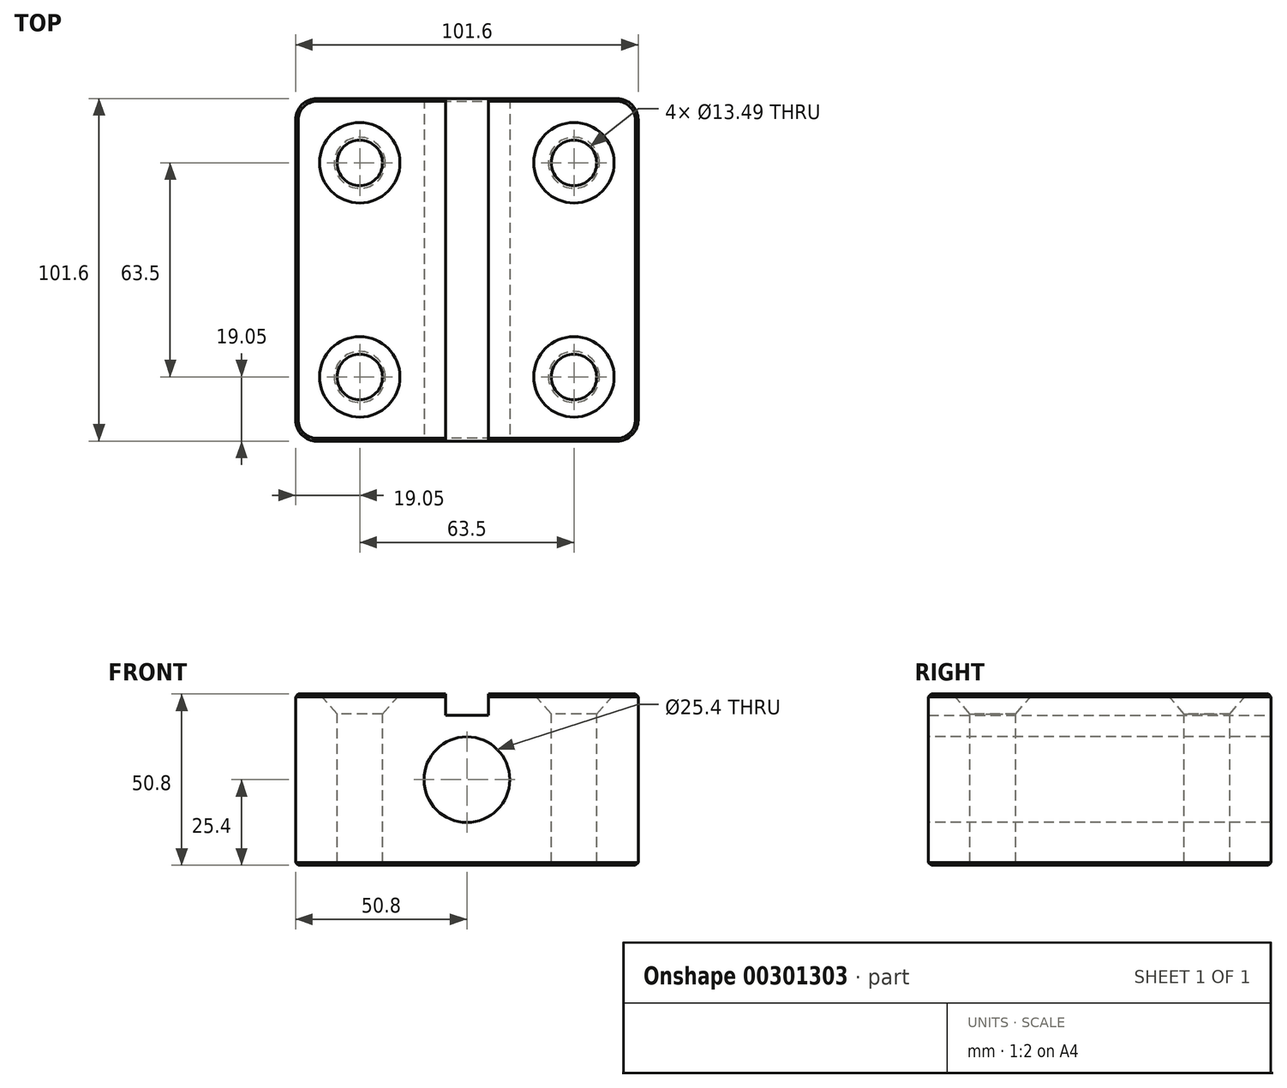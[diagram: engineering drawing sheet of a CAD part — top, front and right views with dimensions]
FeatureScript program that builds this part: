
annotation { "Feature Type Name" : "Feature", "Feature Type Description" : "" }
export const myFeature = defineFeature(function(context is Context, id is Id, definition is map)
    precondition{}
    {
        {
            var Q0;
            Q0=qCreatedBy(makeId("Front.planeOp"),FACE);
            var sketch = newSketch(context, id + "F0", { "sketchPlane" : qUnion([Q0])});
            skLineSegment(sketch, "E0.bottom", {"start": v(-50.8, 25.4) * mm, "end": v(50.8, 25.4) * mm});
            skLineSegment(sketch, "E0.top", {"start": v(-50.8, -25.4) * mm, "end": v(50.8, -25.4) * mm});
            skLineSegment(sketch, "E0.left", {"start": v(-50.8, 25.4) * mm, "end": v(-50.8, -25.4) * mm});
            skLineSegment(sketch, "E0.right", {"start": v(50.8, 25.4) * mm, "end": v(50.8, -25.4) * mm});
            skLineSegment(sketch, "E1.bottom", {"start": v(-6.35, 25.4) * mm, "end": v(6.45, 25.4) * mm});
            skLineSegment(sketch, "E1.top", {"start": v(-6.35, 19.05) * mm, "end": v(6.45, 19.05) * mm});
            skLineSegment(sketch, "E1.left", {"start": v(-6.35, 25.4) * mm, "end": v(-6.35, 19.05) * mm});
            skLineSegment(sketch, "E1.right", {"start": v(6.45, 25.4) * mm, "end": v(6.45, 19.05) * mm});
            skSolve(sketch);
        }
        {
            var Q0;
            Q0=makeQuery(id+"F0.imprint","IMPRINT",FACE,{"disambiguationData":[TD([[makeQuery(id+"F0.imprint","IMPRINT",EDGE,{"derivedFrom":sQuery(id+"F0.wireOp",EDGE,"E0.bottom")}),-1.0]])]});
            extrude(context, id + "F1", {"entities" : qUnion([Q0]), "endBound" : BoundingType.SYMMETRIC, "depth" : 101.6 * mm});
        }
        {
            var Q0;
            Q0=makeQuery(id+"F1.opExtrude","SWEPT_FACE",FACE,{"disambiguationData":[OSD([sQuery(id+"F0.wireOp",EDGE,"E0.bottom")])]});
            var sketch = newSketch(context, id + "F2", { "sketchPlane" : qUnion([Q0])});
            skPoint(sketch, "E2", {"position": v(-31.75, 31.75) * mm});
            skPoint(sketch, "E3.MirrorP", {"position": v(-31.75, -31.75) * mm});
            skPoint(sketch, "E4.MirrorP", {"position": v(31.75, 31.75) * mm});
            skPoint(sketch, "E5.MirrorP", {"position": v(31.75, -31.75) * mm});
            skSolve(sketch);
        }
        {
            var Q0;
            Q0=sQuery(id+"F2.wireOp",VERTEX,"E2");
            var Q1;
            Q1=sQuery(id+"F2.wireOp",VERTEX,"E4.MirrorP");
            var Q2;
            Q2=sQuery(id+"F2.wireOp",VERTEX,"E3.MirrorP");
            var Q3;
            Q3=sQuery(id+"F2.wireOp",VERTEX,"E5.MirrorP");
            var Q4;
            Q4=makeQuery(id+"F1.opExtrude","SWEPT_BODY",BODY,{"disambiguationData":[OSD([sQuery(id+"F0.wireOp",EDGE,"E0.bottom"),sQuery(id+"F0.wireOp",EDGE,"E0.top"),sQuery(id+"F0.wireOp",EDGE,"E0.left"),sQuery(id+"F0.wireOp",EDGE,"E0.right")])]});
            hole(context, id + "F3", {"style" : HoleStyle.C_SINK, "endStyle" : HoleEndStyle.THROUGH, "standardTappedOrClearance" : lookupTablePath({ "standard" : "ANSI", "fit" : "Normal (ASME)", "size" : "1/2", "type" : "Clearance" }), "standardBlindInLast" : lookupTablePath({ "fit" : "Free", "standard" : "ANSI", "size" : "1/2", "type" : "Clearance" }), "holeDiameter" : 13.5 * mm, "cSinkDiameter" : 23.83 * mm, "cSinkAngle" : 82 * degree, "tappedDepth" : 12.7 * mm, "tapClearance" : 3, "locations" : qUnion([Q0, Q1, Q2, Q3]), "scope" : qUnion([Q4])});
        }
        {
            var Q0;
            Q0=makeQuery(id+"F1.opExtrude","CAP_EDGE",EDGE,{"disambiguationData":[OSD([sQuery(id+"F0.wireOp",EDGE,"E0.right")])],"isStart":true});
            var Q1;
            Q1=makeQuery(id+"F1.opExtrude","CAP_EDGE",EDGE,{"disambiguationData":[OSD([sQuery(id+"F0.wireOp",EDGE,"E0.right")])],"isStart":false});
            var Q2;
            Q2=makeQuery(id+"F1.opExtrude","CAP_EDGE",EDGE,{"disambiguationData":[OSD([sQuery(id+"F0.wireOp",EDGE,"E0.left")])],"isStart":false});
            var Q3;
            Q3=makeQuery(id+"F1.opExtrude","CAP_EDGE",EDGE,{"disambiguationData":[OSD([sQuery(id+"F0.wireOp",EDGE,"E0.left")])],"isStart":true});
            fillet(context, id + "F4", {"entities" : qUnion([Q0, Q1, Q2, Q3]), "radius" : 6.35 * mm, "tangentPropagation" : true, "allowEdgeOverflow" : false});
        }
        {
            var Q0;
            Q0=makeQuery(id+"F1.opExtrude","SWEPT_EDGE",EDGE,{"disambiguationData":[OSD([sQuery(id+"F0.wireOp",EDGE,"E0.bottom"),sQuery(id+"F0.wireOp",EDGE,"E0.left")])]});
            var Q1;
            Q1=makeQuery(id+"F1.opExtrude","SWEPT_EDGE",EDGE,{"disambiguationData":[OSD([sQuery(id+"F0.wireOp",EDGE,"E0.bottom"),sQuery(id+"F0.wireOp",EDGE,"E0.right")])]});
            var Q2;
            Q2=makeQuery(id+"F1.opExtrude","CAP_EDGE",EDGE,{"disambiguationData":[OSD([sQuery(id+"F0.wireOp",EDGE,"E0.bottom")])],"isStart":true});
            var Q3;
            Q3=makeQuery(id+"F1.opExtrude","CAP_EDGE",EDGE,{"disambiguationData":[OSD([sQuery(id+"F0.wireOp",EDGE,"E0.bottom")])],"isStart":false});
            var Q4;
            Q4=makeQuery(id+"F1.opExtrude","SWEPT_FACE",FACE,{"disambiguationData":[OSD([sQuery(id+"F0.wireOp",EDGE,"E0.top")])]});
            chamfer(context, id + "F5", {"entities" : qUnion([Q0, Q1, Q2, Q3, Q4]), "width" : 0.81 * mm, "tangentPropagation" : true});
        }
        {
            var Q0;
            Q0=makeQuery(id+"F1.opExtrude","CAP_FACE",FACE,{"disambiguationData":[OSD([sQuery(id+"F0.wireOp",EDGE,"E0.bottom"),sQuery(id+"F0.wireOp",EDGE,"E0.top"),sQuery(id+"F0.wireOp",EDGE,"E0.left"),sQuery(id+"F0.wireOp",EDGE,"E0.right")])],"isStart":false});
            var sketch = newSketch(context, id + "F6", { "sketchPlane" : qUnion([Q0])});
            skPoint(sketch, "E6", {"position": v(0, 0) * mm});
            skSolve(sketch);
        }
        {
            var Q0;
            Q0=sQuery(id+"F6.wireOp",VERTEX,"E6");
            var Q1;
            Q1=makeQuery(id+"F1.opExtrude","SWEPT_BODY",BODY,{"disambiguationData":[OSD([sQuery(id+"F0.wireOp",EDGE,"E0.bottom"),sQuery(id+"F0.wireOp",EDGE,"E0.top"),sQuery(id+"F0.wireOp",EDGE,"E0.left"),sQuery(id+"F0.wireOp",EDGE,"E0.right")])]});
            hole(context, id + "F7", {"style" : HoleStyle.SIMPLE, "endStyle" : HoleEndStyle.THROUGH, "holeDiameter" : 25.4 * mm, "tappedDepth" : 12.7 * mm, "tapClearance" : 3, "locations" : qUnion([Q0]), "scope" : qUnion([Q1])});
        }
    });
